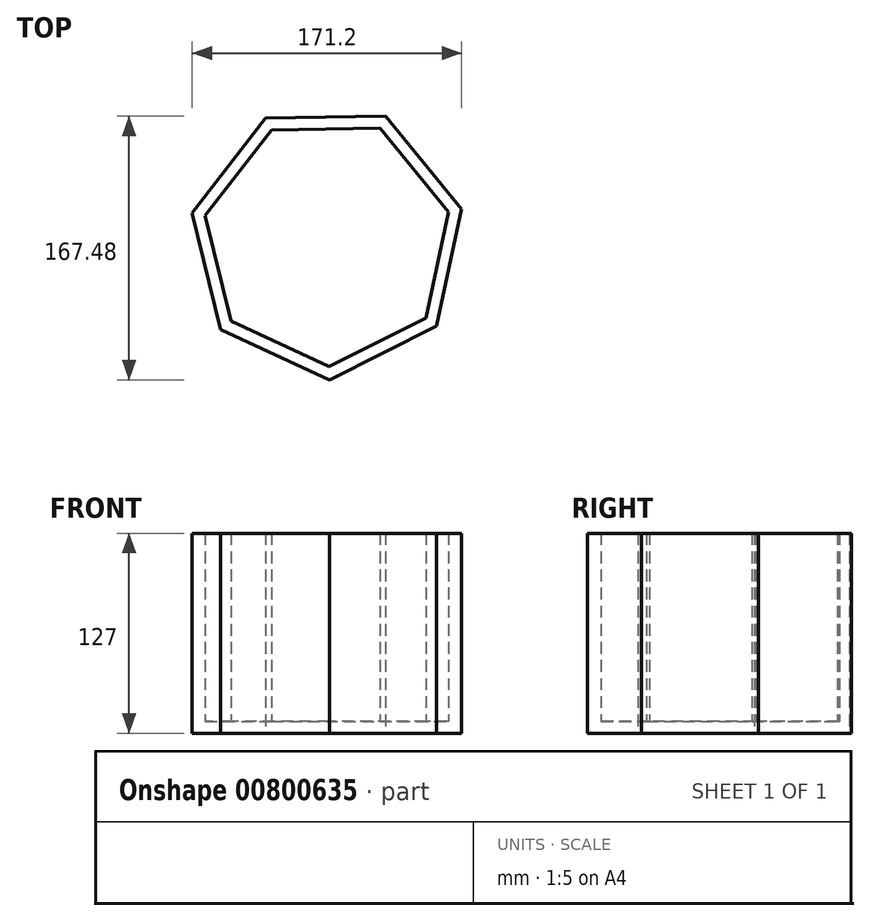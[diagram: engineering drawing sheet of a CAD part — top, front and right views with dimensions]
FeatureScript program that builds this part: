
annotation { "Feature Type Name" : "Feature", "Feature Type Description" : "" }
export const myFeature = defineFeature(function(context is Context, id is Id, definition is map)
    precondition{}
    {
        {
            var Q0;
            Q0=qCreatedBy(makeId("Top.planeOp"),FACE);
            var sketch = newSketch(context, id + "F0", { "sketchPlane" : qUnion([Q0])});
            skCircle(sketch, "E0.cCircle", {"center": v(0, 0) * mm, "radius": 79.12 * mm, "construction": true});
            skLineSegment(sketch, "E0.0", {"start": v(-85.9, 18.25) * mm, "end": v(-39.28, 78.53) * mm});
            skLineSegment(sketch, "E0.1", {"start": v(-39.28, 78.53) * mm, "end": v(36.9, 79.68) * mm});
            skLineSegment(sketch, "E0.2", {"start": v(36.9, 79.68) * mm, "end": v(85.3, 20.82) * mm});
            skLineSegment(sketch, "E0.3", {"start": v(85.3, 20.82) * mm, "end": v(69.47, -53.71) * mm});
            skLineSegment(sketch, "E0.4", {"start": v(69.47, -53.71) * mm, "end": v(1.32, -87.8) * mm});
            skLineSegment(sketch, "E0.5", {"start": v(1.32, -87.8) * mm, "end": v(-67.82, -55.78) * mm});
            skLineSegment(sketch, "E0.6", {"start": v(-67.82, -55.78) * mm, "end": v(-85.9, 18.25) * mm});
            skPoint(sketch, "E0.0.midPoint", {"position": v(-62.59, 48.4) * mm});
            skSolve(sketch);
        }
        {
            var Q0;
            Q0 = qSketchRegion(id + "F0", true);
            extrude(context, id + "F1", {"entities" : qUnion([Q0]), "depth" : 127 * mm, "offsetDistance" : 25.4 * mm});
        }
        {
            var Q0;
            Q0=makeQuery(id+"F1.opExtrude","CAP_FACE",FACE,{"disambiguationData":[OSD([sQuery(id+"F0.wireOp",EDGE,"E0.0"),sQuery(id+"F0.wireOp",EDGE,"E0.1"),sQuery(id+"F0.wireOp",EDGE,"E0.2"),sQuery(id+"F0.wireOp",EDGE,"E0.3"),sQuery(id+"F0.wireOp",EDGE,"E0.4"),sQuery(id+"F0.wireOp",EDGE,"E0.5"),sQuery(id+"F0.wireOp",EDGE,"E0.6")])],"isStart":false});
            shell(context, id + "F2", {"entities" : qUnion([Q0]), "thickness" : 7.62 * mm});
        }
    });
